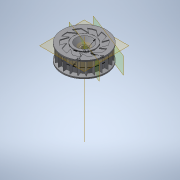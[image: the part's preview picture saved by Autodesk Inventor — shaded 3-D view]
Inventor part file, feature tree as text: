
AUTODESK INVENTOR PART (.ipt)
format: ipt  version: 2020 (Build 240168000, 168)  size: 450,048 bytes
history: native  units: mm
features: reference x80, other x8, extrude x7, sketch x6, plane x4, pattern_circular x2, projected_geometry x2, revolve x1, chamfer x1
ambient origin geometry x8: Origin, YZ Plane, XZ Plane, XY Plane, X Axis, Y Axis, Z Axis, Center Point
bodies: Solid1 (feature_tree)
feature tree (111):
  extrude  "Extrusion1"  Depth=45.0mm
  plane  "Work Plane3"
  revolve  "Revolution1"  [1 undecoded]
  sketch  "Sketch3"  dims[d2=20.0mm d3=10.5mm d4=9.0mm d5=0.0mm d6=0.0mm]
  plane  "Work Plane4"
  other  "Work Axis1"
  extrude  "Extrusion8"  Depth=1.5mm
  pattern_circular  "Circular Pattern3"  [2 undecoded]
  sketch  "Sketch6"  dims[d7=1.5mm d8=1.5mm]
  extrude  "Extrusion4"  Depth=3.0mm
  extrude  "Extrusion5"  [1 undecoded]
  extrude  "Extrusion6"  Depth=14.5mm TaperAngle=0.0deg
  extrude  "Extrusion7"  Depth=9.5mm TaperAngle=0.0deg
  pattern_circular  "Circular Pattern2"  [2 undecoded]
  chamfer  "Chamfer1"  Distance=4.0mm
  extrude  "Extrusion12"  Depth=3.0mm
  sketch  "Sketch1"  dims[d0=0.3mm d1=45.0mm]
  reference  "Reference1"
  reference  "Reference2"
  reference  "Reference3"
  reference  "Reference4"
  reference  "Reference5"
  reference  "Reference6"
  reference  "Reference7"
  reference  "Reference8"
  reference  "Reference9"
  reference  "Reference10"
  reference  "Reference11"
  reference  "Reference12"
  reference  "Reference13"
  reference  "Reference14"
  reference  "Reference15"
  reference  "Reference16"
  reference  "Reference17"
  reference  "Reference18"
  reference  "Reference19"
  reference  "Reference20"
  reference  "Reference21"
  reference  "Reference22"
  reference  "Reference23"
  reference  "Reference24"
  reference  "Reference25"
  reference  "Reference26"
  reference  "Reference27"
  reference  "Reference28"
  reference  "Reference29"
  reference  "Reference30"
  reference  "Reference31"
  reference  "Reference32"
  reference  "Reference33"
  reference  "Reference34"
  reference  "Reference35"
  reference  "Reference36"
  reference  "Reference37"
  reference  "Reference38"
  reference  "Reference39"
  reference  "Reference40"
  reference  "Reference41"
  reference  "Reference42"
  reference  "Reference43"
  reference  "Reference44"
  reference  "Reference45"
  reference  "Reference46"
  reference  "Reference47"
  reference  "Reference48"
  reference  "Reference49"
  reference  "Reference50"
  reference  "Reference51"
  reference  "Reference52"
  reference  "Reference53"
  reference  "Reference54"
  reference  "Reference55"
  reference  "Reference56"
  reference  "Reference57"
  reference  "Reference58"
  reference  "Reference59"
  reference  "Reference60"
  reference  "Reference61"
  reference  "Reference62"
  reference  "Reference63"
  reference  "Reference64"
  reference  "Reference65"
  reference  "Reference66"
  reference  "Reference67"
  reference  "Reference68"
  reference  "Reference69"
  reference  "Reference70"
  reference  "Reference71"
  reference  "Reference72"
  reference  "Reference73"
  reference  "Reference74"
  reference  "Reference75"
  reference  "Reference76"
  reference  "Reference77"
  reference  "Reference78"
  reference  "Reference79"
  reference  "Reference80"
  plane  "Work Plane1"
  plane  "Work Plane2"
  projected_geometry  "Projected Loop1"
  sketch  "Sketch7"  dims[d9=4.0mm]
  projected_geometry  "Projected Loop2"
  sketch  "Sketch8"  dims[d13=90.0deg]
  sketch  "Sketch12"  dims[d14=3.0mm d15=1.25mm d16=1.25mm d17=-3.5mm d26=14.5mm d27=0.0mm d28=9.5mm d29=0.0mm d30=6.0mm d31=4.0mm d32=0.0mm d34=3.0mm d36=3.0mm d37=90.0deg d38=7.0mm d39=1.0mm d40=0.0mm d41=100.0mm d42=360.0deg d44=5.5mm d45=5.5mm d46=45.0deg d53=19.0mm d54=0.0mm d55=220.0mm d56=360.0deg d61=44.0mm d62=2.5mm d63=8.776542mm d65=12.283861mm d71=10.0mm d72=0.0mm d73=3.0mm d74=3.0mm d77=30.0mm]
  other  "<userpath>\Desktop\3d\scanning-robot\Assembly1.iam"
  other  "Assembly1.iam"
  other  "Tower Pro MG90S Micro servo:2"
  other  "Цилиндрическое зубчатое зацепление:5"
  other  "Цилиндрическое зубчатое зацепление2:1"
  other  "Assembly1"
  other  "base:1"
note: 6 required parameter values undecoded (feature->parameter linkage not recoverable at this tier; creation-order binding heuristic only, values carry confidence <= 0.55)